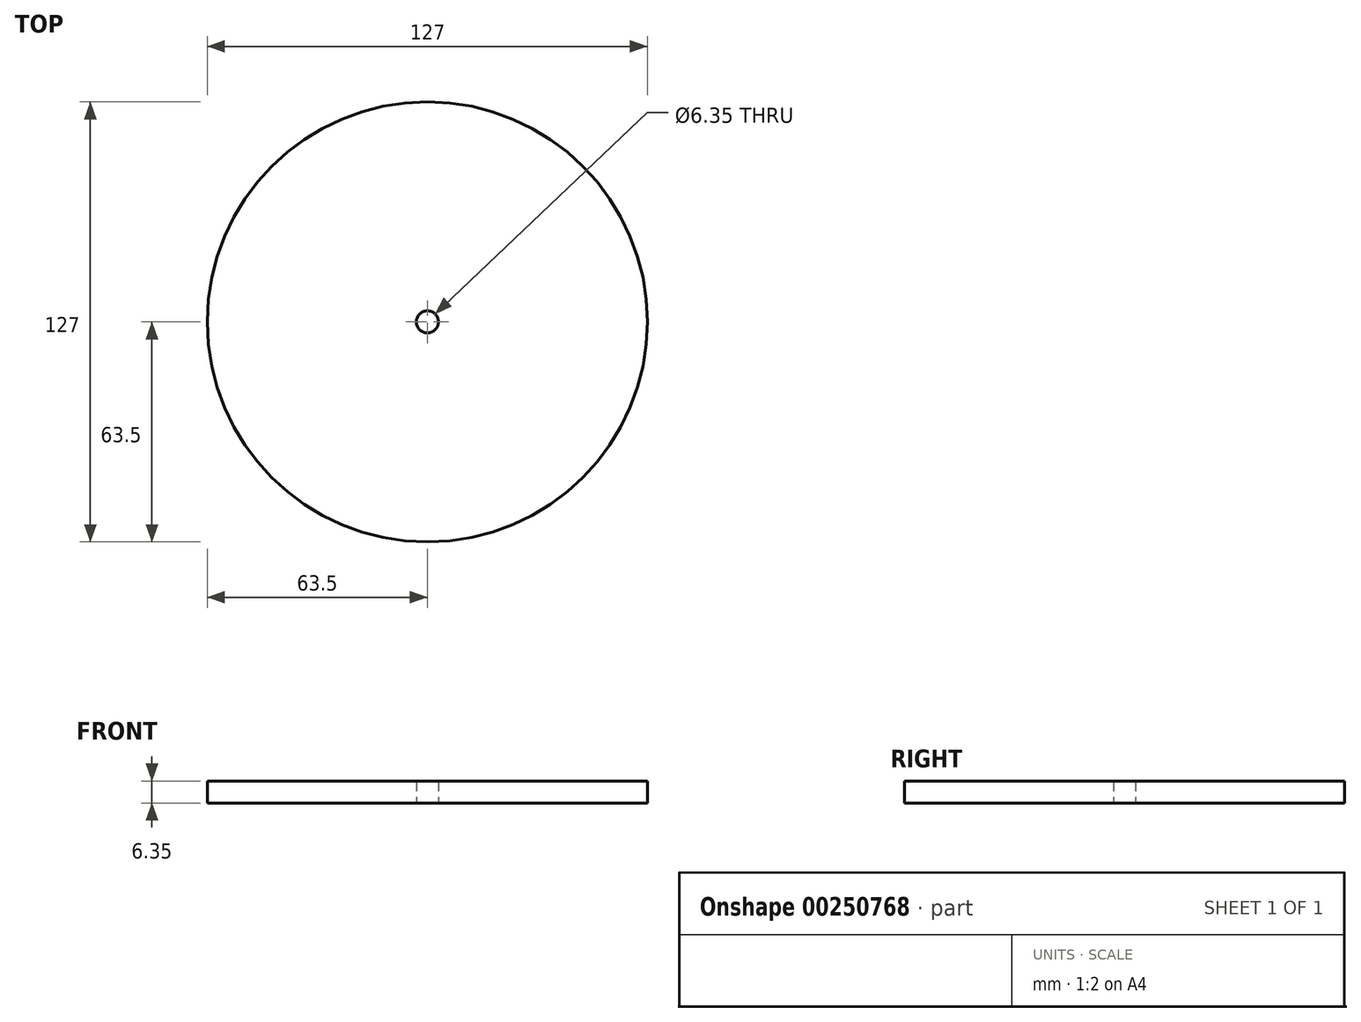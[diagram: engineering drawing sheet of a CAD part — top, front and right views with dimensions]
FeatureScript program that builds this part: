
annotation { "Feature Type Name" : "Feature", "Feature Type Description" : "" }
export const myFeature = defineFeature(function(context is Context, id is Id, definition is map)
    precondition{}
    {
        {
            var Q0;
            Q0=qCreatedBy(makeId("Top.planeOp"),FACE);
            var sketch = newSketch(context, id + "F0", { "sketchPlane" : qUnion([Q0])});
            skCircle(sketch, "E0", {"center": v(0, 0) * mm, "radius": 3.18 * mm});
            skCircle(sketch, "E1", {"center": v(0, 0) * mm, "radius": 63.5 * mm});
            skSolve(sketch);
        }
        {
            var Q0;
            Q0=makeQuery(id+"F0.imprint","IMPRINT",FACE,{"disambiguationData":[TD([[makeQuery(id+"F0.imprint","IMPRINT",EDGE,{"derivedFrom":sQuery(id+"F0.wireOp",EDGE,"E0")}),-1.0]])]});
            extrude(context, id + "F1", {"entities" : qUnion([Q0]), "depth" : 6.35 * mm});
        }
    });
